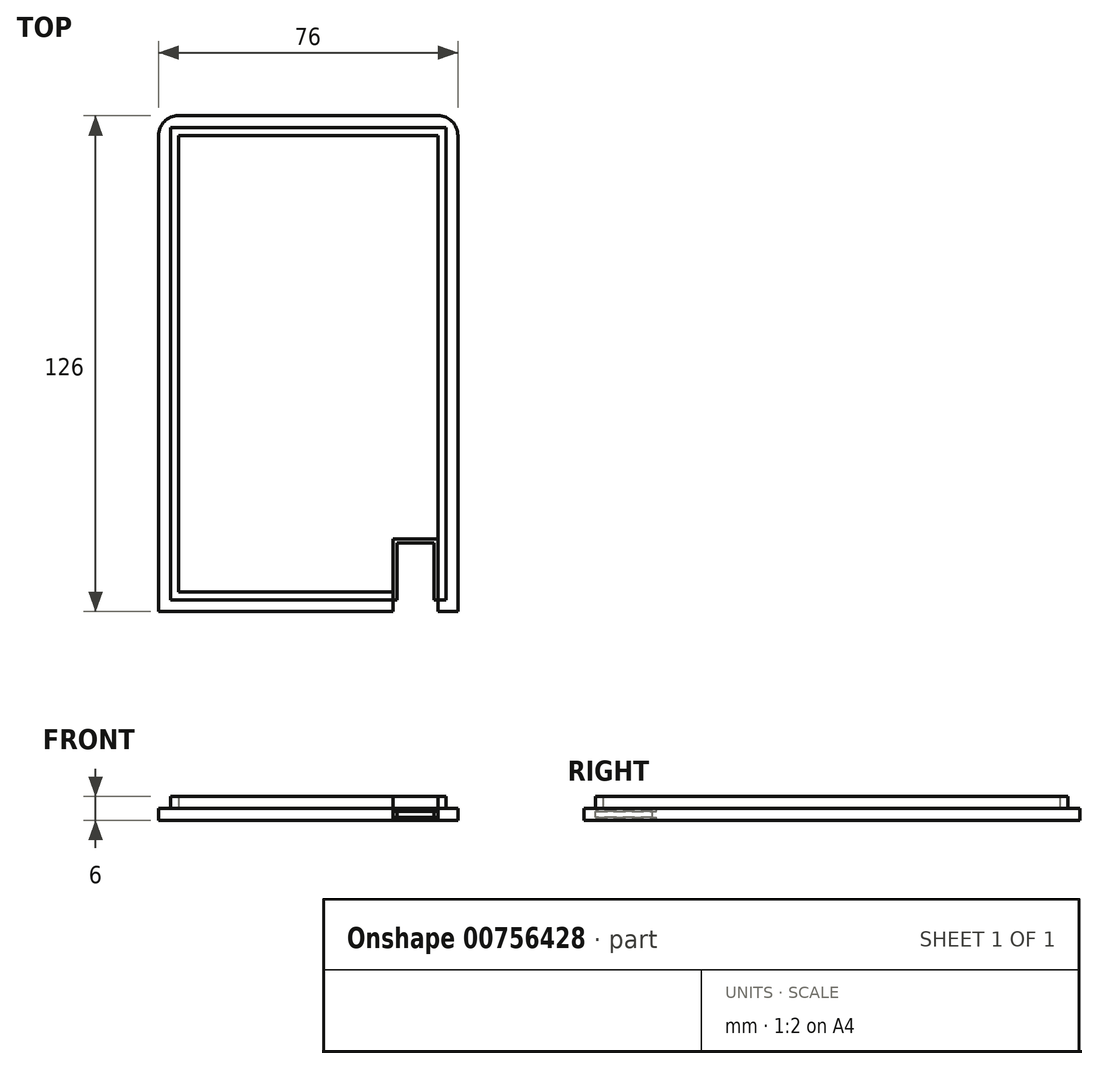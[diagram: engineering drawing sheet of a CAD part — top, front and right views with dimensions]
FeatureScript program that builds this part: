
annotation { "Feature Type Name" : "Feature", "Feature Type Description" : "" }
export const myFeature = defineFeature(function(context is Context, id is Id, definition is map)
    precondition{}
    {
        {
            var Q0;
            Q0=qCreatedBy(makeId("Top.planeOp"),FACE);
            var sketch = newSketch(context, id + "F0", { "sketchPlane" : qUnion([Q0])});
            skLineSegment(sketch, "E0", {"start": v(-38, 63) * mm, "end": v(38, 63) * mm});
            skLineSegment(sketch, "E1", {"start": v(38, 63) * mm, "end": v(38, -63) * mm});
            skLineSegment(sketch, "E2", {"start": v(38, -63) * mm, "end": v(-38, -63) * mm});
            skLineSegment(sketch, "E3", {"start": v(-38, -63) * mm, "end": v(-38, 63) * mm});
            skLineSegment(sketch, "E4", {"start": v(-35, 60) * mm, "end": v(35, 60) * mm});
            skLineSegment(sketch, "E5", {"start": v(35, 60) * mm, "end": v(35, -60) * mm});
            skLineSegment(sketch, "E6", {"start": v(35, -60) * mm, "end": v(-35, -60) * mm});
            skLineSegment(sketch, "E7", {"start": v(-35, -60) * mm, "end": v(-35, 60) * mm});
            skLineSegment(sketch, "E8", {"start": v(-33, 58) * mm, "end": v(33, 58) * mm});
            skLineSegment(sketch, "E9", {"start": v(33, 58) * mm, "end": v(33, -58) * mm});
            skLineSegment(sketch, "E10", {"start": v(33, -58) * mm, "end": v(-33, -58) * mm});
            skLineSegment(sketch, "E11", {"start": v(-33, -58) * mm, "end": v(-33, 58) * mm});
            skSolve(sketch);
        }
        {
            var Q0;
            Q0=makeQuery(id+"F0.imprint","IMPRINT",FACE,{"disambiguationData":[TD([[makeQuery(id+"F0.imprint","IMPRINT",EDGE,{"derivedFrom":sQuery(id+"F0.wireOp",EDGE,"E4")}),-1.0]])]});
            extrude(context, id + "F1", {"entities" : qUnion([Q0]), "depth" : 6 * mm, "offsetDistance" : 25 * mm});
        }
        {
            var Q0;
            Q0=makeQuery(id+"F0.imprint","IMPRINT",FACE,{"disambiguationData":[TD([[makeQuery(id+"F0.imprint","IMPRINT",EDGE,{"derivedFrom":sQuery(id+"F0.wireOp",EDGE,"E0")}),-1.0]])]});
            var Q1;
            Q1=makeQuery(id+"F0.imprint","IMPRINT",FACE,{"disambiguationData":[TD([[makeQuery(id+"F0.imprint","IMPRINT",EDGE,{"derivedFrom":sQuery(id+"F0.wireOp",EDGE,"E8")}),-1.0]])]});
            extrude(context, id + "F2", {"entities" : qUnion([Q0, Q1]), "operationType" : NewBodyOperationType.ADD, "depth" : 3 * mm, "offsetDistance" : 25 * mm});
        }
        {
            var Q0;
            Q0=makeQuery(id+"F2.opExtrude","SWEPT_EDGE",EDGE,{"disambiguationData":[OSD([sQuery(id+"F0.wireOp",EDGE,"E0"),sQuery(id+"F0.wireOp",EDGE,"E3")])]});
            var Q1;
            Q1=makeQuery(id+"F2.opExtrude","SWEPT_EDGE",EDGE,{"disambiguationData":[OSD([sQuery(id+"F0.wireOp",EDGE,"E0"),sQuery(id+"F0.wireOp",EDGE,"E1")])]});
            fillet(context, id + "F3", {"entities" : qUnion([Q0, Q1]), "radius" : 5 * mm, "tangentPropagation" : true, "allowEdgeOverflow" : false});
        }
        {
            var Q0;
            Q0=makeQuery(id+"F2.opExtrude","CAP_FACE",FACE,{"disambiguationData":[OSD([sQuery(id+"F0.wireOp",EDGE,"E8"),sQuery(id+"F0.wireOp",EDGE,"E9"),sQuery(id+"F0.wireOp",EDGE,"E10"),sQuery(id+"F0.wireOp",EDGE,"E11")])],"isStart":false});
            var sketch = newSketch(context, id + "F4", { "sketchPlane" : qUnion([Q0])});
            skLineSegment(sketch, "E12", {"start": v(33, -44.5) * mm, "end": v(21.5, -44.5) * mm});
            skLineSegment(sketch, "E13", {"start": v(21.5, -44.5) * mm, "end": v(21.5, -58) * mm});
            skSolve(sketch);
        }
        {
            var Q0;
            {var subQ0=sQuery(id+"F4.wireOp",EDGE,"E12");Q0=makeQuery(id+"F4.imprint","IMPRINT",FACE,{"disambiguationData":[TD([[makeQuery(id+"F4.imprint","IMPRINT",EDGE,{"derivedFrom":subQ0}),1.0]])]});}
            extrude(context, id + "F5", {"entities" : qUnion([Q0]), "operationType" : NewBodyOperationType.REMOVE, "oppositeDirection" : true, "depth" : 25 * mm, "offsetDistance" : 25 * mm});
        }
        {
            var Q0;
            Q0=makeQuery(id+"F5.boolean.opBoolean","COPY",FACE,{"derivedFrom":makeQuery(id+"F5.opExtrude","SWEPT_FACE",FACE,{"disambiguationData":[OSD([sQuery(id+"F4.wireOp",EDGE,"E12")])]})});
            var sketch = newSketch(context, id + "F6", { "sketchPlane" : qUnion([Q0])});
            skLineSegment(sketch, "E14", {"start": v(33, 1.5) * mm, "end": v(21.5, 1.5) * mm, "construction": true});
            skLineSegment(sketch, "E15", {"start": v(33, 2.25) * mm, "end": v(21.5, 2.25) * mm});
            skLineSegment(sketch, "E16", {"start": v(21.5, 0.75) * mm, "end": v(33, 0.75) * mm});
            skSolve(sketch);
        }
        {
            var Q0;
            Q0=makeQuery(id+"F5.boolean.opBoolean","COPY",FACE,{"derivedFrom":makeQuery(id+"F5.opExtrude","SWEPT_FACE",FACE,{"disambiguationData":[OSD([sQuery(id+"F4.wireOp",EDGE,"E13")])]})});
            var sketch = newSketch(context, id + "F7", { "sketchPlane" : qUnion([Q0])});
            skLineSegment(sketch, "E17", {"start": v(-44.5, 1.5) * mm, "end": v(-58, 1.5) * mm, "construction": true});
            skLineSegment(sketch, "E18", {"start": v(-44.5, 2.25) * mm, "end": v(-58, 2.25) * mm});
            skLineSegment(sketch, "E19", {"start": v(-44.5, 0.75) * mm, "end": v(-58, 0.75) * mm});
            skSolve(sketch);
        }
        {
            var Q0;
            {var subQ0=sQuery(id+"F0.wireOp",EDGE,"E9");Q0=makeQuery(id+"F5.boolean.opBoolean","MERGE",FACE,{"derivedFrom":[makeQuery(id+"F1.opExtrude","SWEPT_FACE",FACE,{"disambiguationData":[OSD([subQ0])]}),makeQuery(id+"F5.opExtrude","SWEPT_FACE",FACE,{"disambiguationData":[OSD([subQ0])]})]});}
            var sketch = newSketch(context, id + "F8", { "sketchPlane" : qUnion([Q0])});
            skLineSegment(sketch, "E20", {"start": v(44.5, 1.5) * mm, "end": v(58, 1.5) * mm, "construction": true});
            skLineSegment(sketch, "E21", {"start": v(44.5, 2.25) * mm, "end": v(58, 2.25) * mm});
            skLineSegment(sketch, "E22", {"start": v(44.5, 0.75) * mm, "end": v(58, 0.75) * mm});
            skSolve(sketch);
        }
        {
            var Q0;
            {var subQ0=sQuery(id+"F8.wireOp",EDGE,"E21");Q0=makeQuery(id+"F8.imprint","IMPRINT",FACE,{"disambiguationData":[TD([[makeQuery(id+"F8.imprint","IMPRINT",EDGE,{"derivedFrom":subQ0}),-1.0]])]});}
            extrude(context, id + "F9", {"entities" : qUnion([Q0]), "operationType" : NewBodyOperationType.ADD, "depth" : 1 * mm, "offsetDistance" : 25 * mm});
        }
        {
            var Q0;
            {var subQ0=sQuery(id+"F6.wireOp",EDGE,"E15");Q0=makeQuery(id+"F6.imprint","IMPRINT",FACE,{"disambiguationData":[TD([[makeQuery(id+"F6.imprint","IMPRINT",EDGE,{"derivedFrom":subQ0}),1.0]])]});}
            extrude(context, id + "F10", {"entities" : qUnion([Q0]), "operationType" : NewBodyOperationType.ADD, "depth" : 1 * mm, "offsetDistance" : 25 * mm});
        }
        {
            var Q0;
            {var subQ0=sQuery(id+"F7.wireOp",EDGE,"E18");Q0=makeQuery(id+"F7.imprint","IMPRINT",FACE,{"disambiguationData":[TD([[makeQuery(id+"F7.imprint","IMPRINT",EDGE,{"derivedFrom":subQ0}),1.0]])]});}
            extrude(context, id + "F11", {"entities" : qUnion([Q0]), "operationType" : NewBodyOperationType.ADD, "depth" : 1 * mm, "offsetDistance" : 25 * mm});
        }
        {
            var Q0;
            {var subQ0=sQuery(id+"F0.wireOp",EDGE,"E10");Q0=makeQuery(id+"F5.boolean.opBoolean","MERGE",FACE,{"derivedFrom":[makeQuery(id+"F1.opExtrude","SWEPT_FACE",FACE,{"disambiguationData":[OSD([subQ0])]}),makeQuery(id+"F5.opExtrude","SWEPT_FACE",FACE,{"disambiguationData":[OSD([subQ0])]})]});}
            var sketch = newSketch(context, id + "F12", { "sketchPlane" : qUnion([Q0])});
            skLineSegment(sketch, "E23", {"start": v(-21.5, 3) * mm, "end": v(-21.5, 6) * mm});
            skSolve(sketch);
        }
        {
            var Q0;
            {var subQ24=sQuery(id+"F12.wireOp",EDGE,"E23");Q0=makeQuery(id+"F12.imprint","IMPRINT",FACE,{"disambiguationData":[TD([[makeQuery(id+"F12.imprint","IMPRINT",EDGE,{"derivedFrom":subQ24}),1.0]])]});}
            extrude(context, id + "F13", {"entities" : qUnion([Q0]), "operationType" : NewBodyOperationType.REMOVE, "oppositeDirection" : true, "depth" : 25 * mm, "offsetDistance" : 25 * mm});
        }
        {
            var Q0;
            {var subQ2=sQuery(id+"F0.wireOp",EDGE,"E3");var subQ16=sQuery(id+"F0.wireOp",EDGE,"E2");Q0=makeQuery(id+"F13.boolean.opBoolean","SPLIT",FACE,{"disambiguationData":[TD([makeQuery(id+"F2.opExtrude","SWEPT_FACE",FACE,{"disambiguationData":[OSD([subQ2])]})])],"derivedFrom":makeQuery(id+"F2.opExtrude","SWEPT_FACE",FACE,{"disambiguationData":[OSD([subQ16])]})});}
            var sketch = newSketch(context, id + "F14", { "sketchPlane" : qUnion([Q0])});
            skLineSegment(sketch, "E24", {"start": v(21.5, 2.25) * mm, "end": v(21.5, 0.75) * mm});
            skSolve(sketch);
        }
        {
            var Q0;
            {var subQ3=sQuery(id+"F0.wireOp",EDGE,"E9");var subQ14=sQuery(id+"F0.wireOp",EDGE,"E2");var subQ22=makeQuery(id+"F1.opExtrude","SWEPT_FACE",FACE,{"disambiguationData":[OSD([subQ3])]});Q0=makeQuery(id+"F13.boolean.opBoolean","SPLIT",FACE,{"disambiguationData":[TD([subQ22])],"derivedFrom":makeQuery(id+"F2.opExtrude","SWEPT_FACE",FACE,{"disambiguationData":[OSD([subQ14])]})});}
            var sketch = newSketch(context, id + "F15", { "sketchPlane" : qUnion([Q0])});
            skLineSegment(sketch, "E25", {"start": v(33, 0.75) * mm, "end": v(33, 2.25) * mm});
            skSolve(sketch);
        }
        {
            var Q0;
            Q0=makeQuery(id+"F14.imprint","IMPRINT",FACE,{"disambiguationData":[TD([[makeQuery(id+"F14.imprint","IMPRINT",EDGE,{"derivedFrom":sQuery(id+"F14.wireOp",EDGE,"E24")}),1.0]])]});
            var Q1;
            Q1=makeQuery(id+"F15.imprint","IMPRINT",FACE,{"disambiguationData":[TD([[makeQuery(id+"F15.imprint","IMPRINT",EDGE,{"derivedFrom":sQuery(id+"F15.wireOp",EDGE,"E25")}),1.0]])]});
            extrude(context, id + "F16", {"entities" : qUnion([Q0, Q1]), "operationType" : NewBodyOperationType.REMOVE, "oppositeDirection" : true, "depth" : 3 * mm, "offsetDistance" : 25 * mm});
        }
    });
